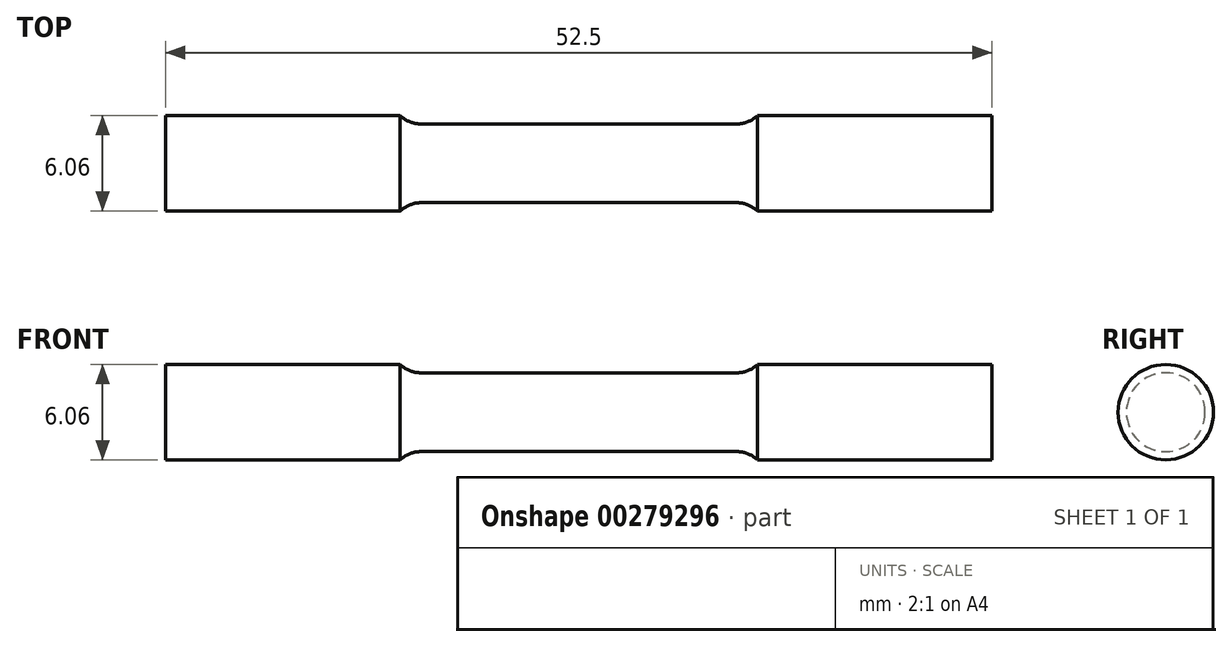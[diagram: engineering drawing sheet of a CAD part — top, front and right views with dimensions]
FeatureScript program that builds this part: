
annotation { "Feature Type Name" : "Feature", "Feature Type Description" : "" }
export const myFeature = defineFeature(function(context is Context, id is Id, definition is map)
    precondition{}
    {
        {
            var Q0;
            Q0=qCreatedBy(makeId("Front.planeOp"),FACE);
            var sketch = newSketch(context, id + "F0", { "sketchPlane" : qUnion([Q0])});
            skLineSegment(sketch, "E0", {"start": v(0, 2.5) * mm, "end": v(10, 2.5) * mm});
            skArc(sketch, "E1", {"start": v(10, 2.5) * mm, "mid": v(10.72, 2.64) * mm, "end": v(11.35, 3.03) * mm});
            skLineSegment(sketch, "E2", {"start": v(11.35, 3.03) * mm, "end": v(26.25, 3.03) * mm});
            skLineSegment(sketch, "E3", {"start": v(26.25, 3.03) * mm, "end": v(26.25, 0) * mm});
            skLineSegment(sketch, "E4.MirrorCS", {"start": v(0, 2.5) * mm, "end": v(-10, 2.5) * mm});
            skLineSegment(sketch, "E5.MirrorCS", {"start": v(-11.35, 3.03) * mm, "end": v(-26.25, 3.03) * mm});
            skArc(sketch, "E6.MirrorCS", {"start": v(-10, 2.5) * mm, "mid": v(-10.72, 2.64) * mm, "end": v(-11.35, 3.03) * mm});
            skLineSegment(sketch, "E7.MirrorCS", {"start": v(-26.25, 3.03) * mm, "end": v(-26.25, 0) * mm});
            skLineSegment(sketch, "E8", {"start": v(-26.25, 0) * mm, "end": v(26.25, 0) * mm});
            skSolve(sketch);
        }
        {
            var Q0;
            Q0 = qSketchRegion(id + "F0", true);
            var Q1;
            Q1=sQuery(id+"F0.wireOp",EDGE,"E8");
            revolve(context, id + "F1", {"entities" : qUnion([Q0]), "axis" : qUnion([Q1]), "revolveType" : RevolveType.FULL});
        }
    });
